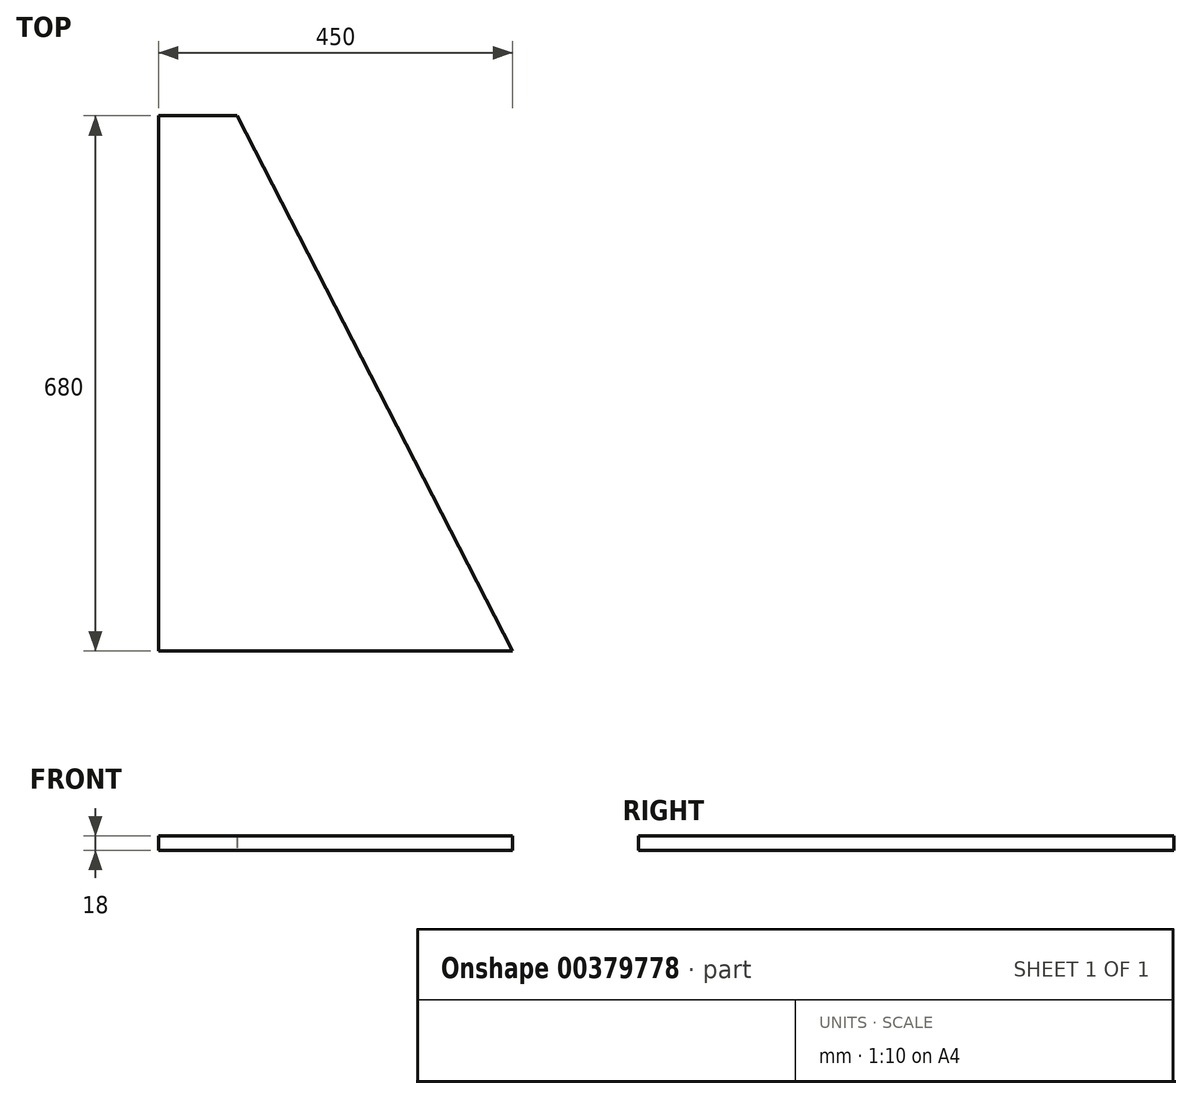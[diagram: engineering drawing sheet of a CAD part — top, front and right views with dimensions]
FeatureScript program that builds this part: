
annotation { "Feature Type Name" : "Feature", "Feature Type Description" : "" }
export const myFeature = defineFeature(function(context is Context, id is Id, definition is map)
    precondition{}
    {
        {
            var Q0;
            Q0=qCreatedBy(makeId("Top.planeOp"),FACE);
            var sketch = newSketch(context, id + "F0", { "sketchPlane" : qUnion([Q0])});
            skLineSegment(sketch, "E0.bottom", {"start": v(-196.07, -204.6) * mm, "end": v(253.93, -204.6) * mm});
            skLineSegment(sketch, "E0.top", {"start": v(-196.07, 475.4) * mm, "end": v(-96.07, 475.4) * mm});
            skLineSegment(sketch, "E0.left", {"start": v(-196.07, -204.6) * mm, "end": v(-196.07, 475.4) * mm});
            skLineSegment(sketch, "E0.right", {"start": v(253.93, -204.6) * mm, "end": v(-96.07, 475.4) * mm});
            skSolve(sketch);
        }
        {
            var Q0;
            Q0=qSketchRegion(id+"F0",true);
            extrude(context, id + "F1", {"entities" : qUnion([Q0]), "depth" : 18 * mm});
        }
    });
